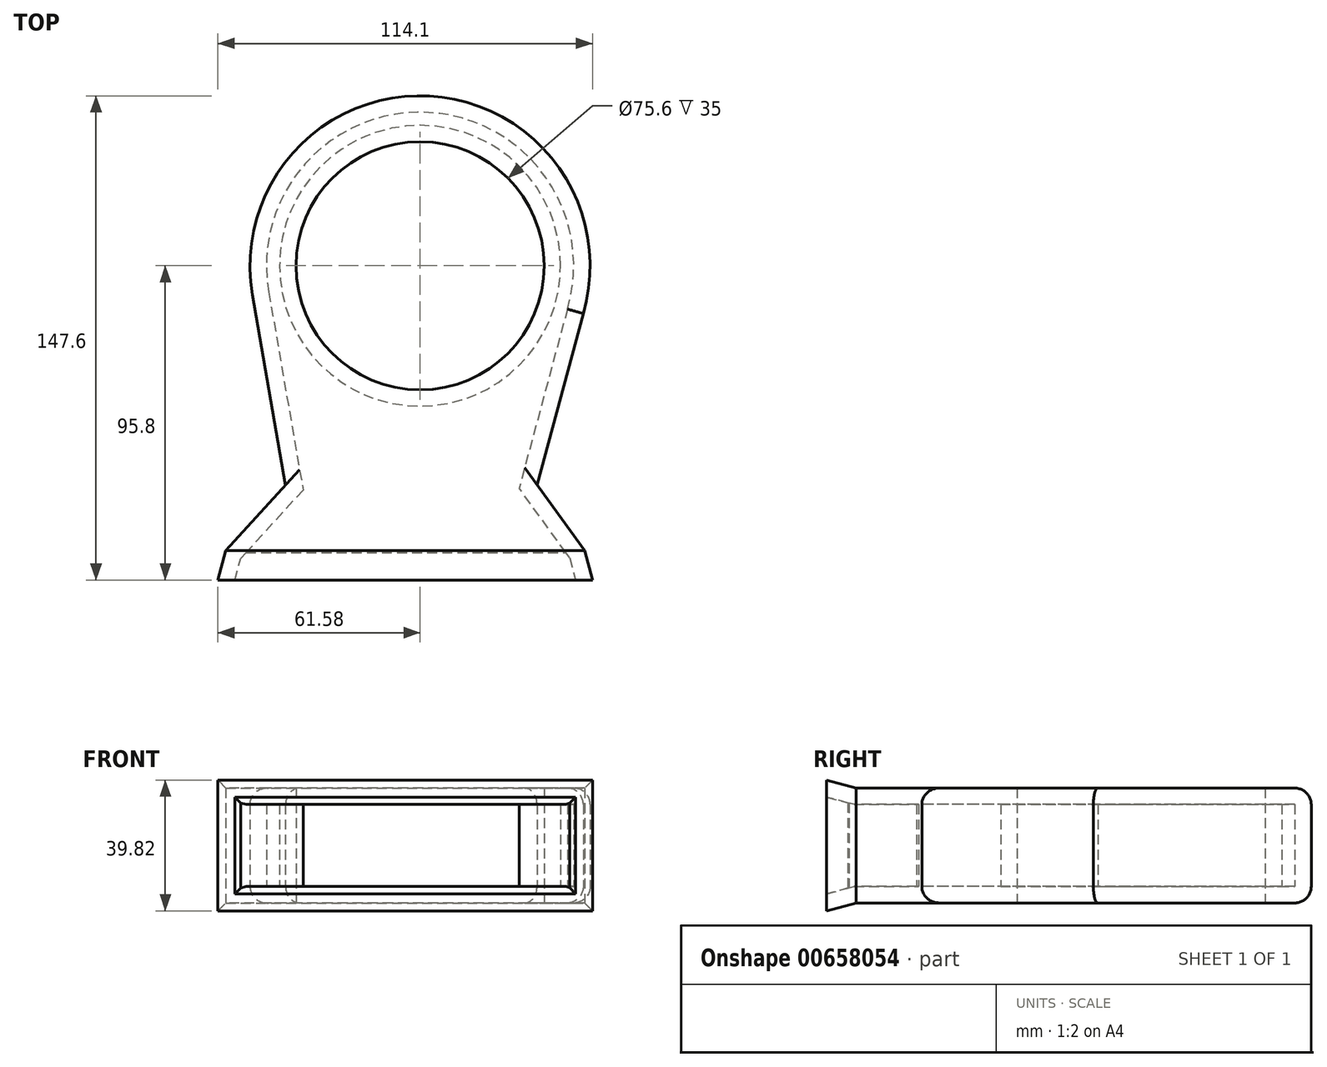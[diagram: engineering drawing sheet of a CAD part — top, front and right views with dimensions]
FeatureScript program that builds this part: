
annotation { "Feature Type Name" : "Feature", "Feature Type Description" : "" }
export const myFeature = defineFeature(function(context is Context, id is Id, definition is map)
    precondition{}
    {
        {
            var Q0;
            Q0=qCreatedBy(makeId("Top.planeOp"),FACE);
            var sketch = newSketch(context, id + "F0", { "sketchPlane" : qUnion([Q0])});
            skCircle(sketch, "E0", {"center": v(0, 0) * mm, "radius": 37.8 * mm});
            skCircle(sketch, "E1", {"center": v(0, 0) * mm, "radius": 51.8 * mm});
            skLineSegment(sketch, "E2.bottom", {"start": v(-40.97, -66.8) * mm, "end": v(35.63, -66.8) * mm});
            skLineSegment(sketch, "E3", {"start": v(-40.97, -66.8) * mm, "end": v(-51.04, -8.86) * mm});
            skLineSegment(sketch, "E4", {"start": v(35.63, -66.8) * mm, "end": v(49.7, -14.57) * mm});
            skLineSegment(sketch, "E5", {"start": v(0, 59.08) * mm, "end": v(0.55, 37.8) * mm, "construction": true});
            skPoint(sketch, "E6.trimOffspring.end.orphan", {"position": v(0, -118.65) * mm});
            skLineSegment(sketch, "E7", {"start": v(0, 0) * mm, "end": v(0, -126.66) * mm, "construction": true});
            skLineSegment(sketch, "E8", {"start": v(-40.97, -66.8) * mm, "end": v(-59.16, -86.8) * mm});
            skLineSegment(sketch, "E9", {"start": v(-59.16, -86.8) * mm, "end": v(50.1, -86.8) * mm});
            skLineSegment(sketch, "E10", {"start": v(50.1, -86.8) * mm, "end": v(35.63, -66.8) * mm});
            skPoint(sketch, "E2.left.end.orphan", {"position": v(-37.5, -118.65) * mm});
            skPoint(sketch, "E2.right.end.orphan", {"position": v(37.5, -118.65) * mm});
            skSolve(sketch);
        }
        {
            var Q0;
            Q0=makeQuery(id+"F0.imprint","IMPRINT",FACE,{"disambiguationData":[TD([[makeQuery(id+"F0.imprint","IMPRINT",EDGE,{"derivedFrom":sQuery(id+"F0.wireOp",EDGE,"E0")}),-1.0]])]});
            var Q1;
            Q1=makeQuery(id+"F0.imprint","IMPRINT",FACE,{"disambiguationData":[TD([[makeQuery(id+"F0.imprint","IMPRINT",EDGE,{"derivedFrom":sQuery(id+"F0.wireOp",EDGE,"E2.bottom")}),1.0]])]});
            var Q2;
            Q2=makeQuery(id+"F0.imprint","IMPRINT",FACE,{"disambiguationData":[TD([[makeQuery(id+"F0.imprint","IMPRINT",EDGE,{"derivedFrom":sQuery(id+"F0.wireOp",EDGE,"E2.bottom")}),-1.0]])]});
            extrude(context, id + "F1", {"entities" : qUnion([Q0, Q1, Q2]), "depth" : 35 * mm, "offsetDistance" : 25 * mm});
        }
        {
            var Q0;
            Q0=makeQuery(id+"F1.opExtrude","CAP_EDGE",EDGE,{"disambiguationData":[OSD([sQuery(id+"F0.wireOp",EDGE,"E1")])],"isStart":false});
            var Q1;
            Q1=makeQuery(id+"F1.opExtrude","CAP_EDGE",EDGE,{"disambiguationData":[OSD([sQuery(id+"F0.wireOp",EDGE,"E1")])],"isStart":true});
            fillet(context, id + "F2", {"entities" : qUnion([Q0, Q1]), "radius" : 5 * mm, "tangentPropagation" : true, "allowEdgeOverflow" : false});
        }
        {
            var Q0;
            Q0=makeQuery(id+"F1.opExtrude","SWEPT_FACE",FACE,{"disambiguationData":[OSD([sQuery(id+"F0.wireOp",EDGE,"E9")])]});
            extrude(context, id + "F3", {"entities" : qUnion([Q0]), "operationType" : NewBodyOperationType.ADD, "depth" : 9 * mm, "offsetDistance" : 25 * mm, "hasDraft" : true, "draftAngle" : 15 * degree});
        }
        {
            var Q0;
            Q0=makeQuery(id+"F3.opExtrude","CAP_FACE",FACE,{"disambiguationData":[OSD([sQuery(id+"F0.wireOp",EDGE,"E9")])],"isStart":false});
            shell(context, id + "F4", {"entities" : qUnion([Q0]), "thickness" : 5 * mm});
        }
    });
